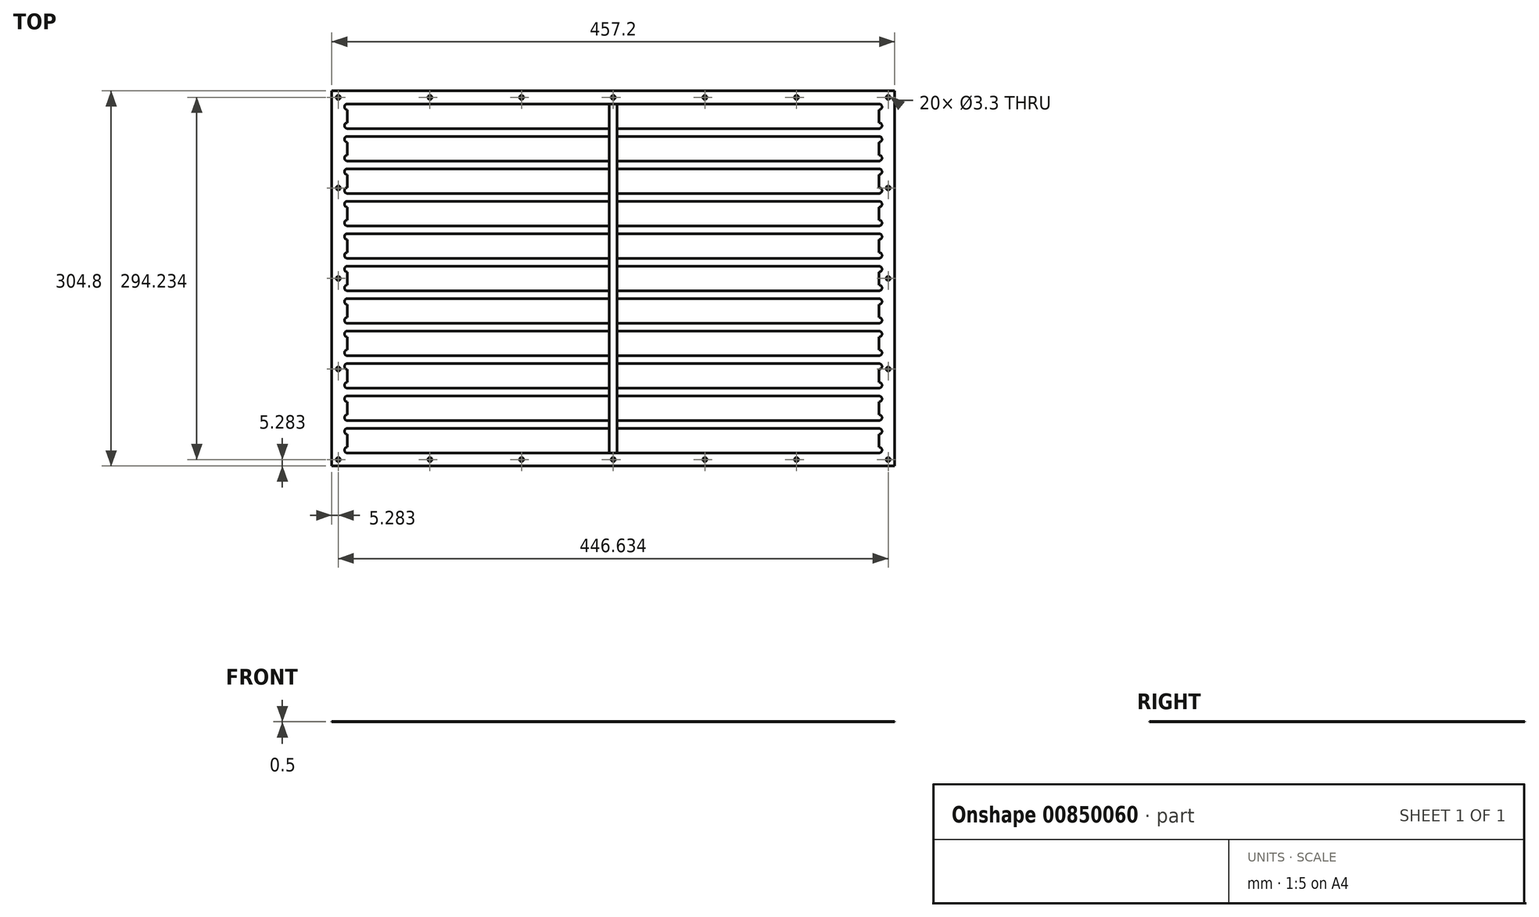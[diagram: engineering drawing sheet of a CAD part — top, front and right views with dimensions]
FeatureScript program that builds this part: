
annotation { "Feature Type Name" : "Feature", "Feature Type Description" : "" }
export const myFeature = defineFeature(function(context is Context, id is Id, definition is map)
    precondition{}
    {
        {
            assignVariable(context, id + "F0", {"name" : "mold_Thickness", "anyValue" : .5});
        }
        {
            assignVariable(context, id + "F1", {"name" : "hole_Depth", "anyValue" : .25});
        }
        {
            var Q0;
            Q0=qCreatedBy(makeId("Top.planeOp"),FACE);
            var sketch = newSketch(context, id + "F2", { "sketchPlane" : qUnion([Q0])});
            skLineSegment(sketch, "E0.bottom", {"start": v(228.6, -152.4) * mm, "end": v(-228.6, -152.4) * mm});
            skLineSegment(sketch, "E0.top", {"start": v(228.6, 152.4) * mm, "end": v(-228.6, 152.4) * mm});
            skLineSegment(sketch, "E0.left", {"start": v(228.6, -152.4) * mm, "end": v(228.6, 152.4) * mm});
            skLineSegment(sketch, "E0.right", {"start": v(-228.6, -152.4) * mm, "end": v(-228.6, 152.4) * mm});
            skPoint(sketch, "E0.middle", {"position": v(0, 0) * mm});
            skSolve(sketch);
        }
        {
            var Q0;
            Q0 = qSketchRegion(id + "F2", true);
            extrude(context, id + "F3", {"entities" : qUnion([Q0]), "depth" : (getVariable(context, 'mold_Thickness')) * mm, "offsetDistance" : 25.4 * mm});
        }
        {
            var Q0;
            Q0=makeQuery(id+"F3.opExtrude","CAP_FACE",FACE,{"disambiguationData":[OSD([sQuery(id+"F2.wireOp",EDGE,"E0.bottom"),sQuery(id+"F2.wireOp",EDGE,"E0.top"),sQuery(id+"F2.wireOp",EDGE,"E0.left"),sQuery(id+"F2.wireOp",EDGE,"E0.right")])],"isStart":false});
            var sketch = newSketch(context, id + "F4", { "sketchPlane" : qUnion([Q0])});
            skLineSegment(sketch, "E1.bottom", {"start": v(-215.9, 141.83) * mm, "end": v(215.9, 141.83) * mm});
            skLineSegment(sketch, "E1.top", {"start": v(-215.9, 121.82) * mm, "end": v(215.9, 121.82) * mm});
            skLineSegment(sketch, "E1.left", {"start": v(-215.9, 141.83) * mm, "end": v(-215.9, 121.82) * mm});
            skLineSegment(sketch, "E1.right", {"start": v(215.9, 141.83) * mm, "end": v(215.9, 121.82) * mm});
            skLineSegment(sketch, "E2.bottom", {"start": v(-215.9, 115.47) * mm, "end": v(215.9, 115.47) * mm});
            skLineSegment(sketch, "E2.top", {"start": v(-215.9, 95.45) * mm, "end": v(215.9, 95.45) * mm});
            skLineSegment(sketch, "E2.left", {"start": v(-215.9, 115.47) * mm, "end": v(-215.9, 95.45) * mm});
            skLineSegment(sketch, "E2.right", {"start": v(215.9, 115.47) * mm, "end": v(215.9, 95.45) * mm});
            skLineSegment(sketch, "E3.bottom", {"start": v(-215.9, 89.1) * mm, "end": v(215.9, 89.1) * mm});
            skLineSegment(sketch, "E3.top", {"start": v(-215.9, 69.09) * mm, "end": v(215.9, 69.09) * mm});
            skLineSegment(sketch, "E3.left", {"start": v(-215.9, 89.1) * mm, "end": v(-215.9, 69.09) * mm});
            skLineSegment(sketch, "E3.right", {"start": v(215.9, 89.1) * mm, "end": v(215.9, 69.09) * mm});
            skLineSegment(sketch, "E4.bottom", {"start": v(-215.9, 62.74) * mm, "end": v(215.9, 62.74) * mm});
            skLineSegment(sketch, "E4.top", {"start": v(-215.9, 42.72) * mm, "end": v(215.9, 42.72) * mm});
            skLineSegment(sketch, "E4.left", {"start": v(-215.9, 62.74) * mm, "end": v(-215.9, 42.72) * mm});
            skLineSegment(sketch, "E4.right", {"start": v(215.9, 62.74) * mm, "end": v(215.9, 42.72) * mm});
            skLineSegment(sketch, "E5.bottom", {"start": v(-215.9, 36.37) * mm, "end": v(215.9, 36.37) * mm});
            skLineSegment(sketch, "E5.top", {"start": v(-215.9, 16.36) * mm, "end": v(215.9, 16.36) * mm});
            skLineSegment(sketch, "E5.left", {"start": v(-215.9, 36.37) * mm, "end": v(-215.9, 16.36) * mm});
            skLineSegment(sketch, "E5.right", {"start": v(215.9, 36.37) * mm, "end": v(215.9, 16.36) * mm});
            skLineSegment(sketch, "E6.bottom", {"start": v(-215.9, 10) * mm, "end": v(215.9, 10) * mm});
            skLineSegment(sketch, "E6.top", {"start": v(-215.9, -10) * mm, "end": v(215.9, -10) * mm});
            skLineSegment(sketch, "E6.left", {"start": v(-215.9, 10) * mm, "end": v(-215.9, -10) * mm});
            skLineSegment(sketch, "E6.right", {"start": v(215.9, 10) * mm, "end": v(215.9, -10) * mm});
            skLineSegment(sketch, "E7.bottom", {"start": v(-215.9, -16.36) * mm, "end": v(215.9, -16.36) * mm});
            skLineSegment(sketch, "E7.top", {"start": v(-215.9, -36.37) * mm, "end": v(215.9, -36.37) * mm});
            skLineSegment(sketch, "E7.left", {"start": v(-215.9, -16.36) * mm, "end": v(-215.9, -36.37) * mm});
            skLineSegment(sketch, "E7.right", {"start": v(215.9, -16.36) * mm, "end": v(215.9, -36.37) * mm});
            skPoint(sketch, "E8.firstSnap0", {"position": v(-215.9, -26.37) * mm});
            skLineSegment(sketch, "E8.bottom", {"start": v(-215.9, -42.72) * mm, "end": v(215.9, -42.72) * mm});
            skLineSegment(sketch, "E8.top", {"start": v(-215.9, -62.74) * mm, "end": v(215.9, -62.74) * mm});
            skLineSegment(sketch, "E8.left", {"start": v(-215.9, -42.72) * mm, "end": v(-215.9, -62.74) * mm});
            skLineSegment(sketch, "E8.right", {"start": v(215.9, -42.72) * mm, "end": v(215.9, -62.74) * mm});
            skLineSegment(sketch, "E9.bottom", {"start": v(-215.9, -69.09) * mm, "end": v(215.9, -69.09) * mm});
            skLineSegment(sketch, "E9.top", {"start": v(-215.9, -89.1) * mm, "end": v(215.9, -89.1) * mm});
            skLineSegment(sketch, "E9.left", {"start": v(-215.9, -69.09) * mm, "end": v(-215.9, -89.1) * mm});
            skLineSegment(sketch, "E9.right", {"start": v(215.9, -69.09) * mm, "end": v(215.9, -89.1) * mm});
            skLineSegment(sketch, "E10.bottom", {"start": v(-215.9, -95.45) * mm, "end": v(215.9, -95.45) * mm});
            skLineSegment(sketch, "E10.top", {"start": v(-215.9, -115.47) * mm, "end": v(215.9, -115.47) * mm});
            skLineSegment(sketch, "E10.left", {"start": v(-215.9, -95.45) * mm, "end": v(-215.9, -115.47) * mm});
            skLineSegment(sketch, "E10.right", {"start": v(215.9, -95.45) * mm, "end": v(215.9, -115.47) * mm});
            skLineSegment(sketch, "E11.bottom", {"start": v(-215.9, -121.82) * mm, "end": v(215.9, -121.82) * mm});
            skLineSegment(sketch, "E11.top", {"start": v(-215.9, -141.83) * mm, "end": v(215.9, -141.83) * mm});
            skLineSegment(sketch, "E11.left", {"start": v(-215.9, -121.82) * mm, "end": v(-215.9, -141.83) * mm});
            skLineSegment(sketch, "E11.right", {"start": v(215.9, -121.82) * mm, "end": v(215.9, -141.83) * mm});
            skSolve(sketch);
        }
        {
            var Q0;
            Q0 = qSketchRegion(id + "F4", true);
            extrude(context, id + "F5", {"entities" : qUnion([Q0]), "operationType" : NewBodyOperationType.REMOVE, "oppositeDirection" : true, "depth" : (getVariable(context, 'hole_Depth')) * mm, "offsetDistance" : 25.4 * mm});
        }
        {
            var Q0;
            Q0=makeQuery(id+"F3.opExtrude","CAP_FACE",FACE,{"disambiguationData":[OSD([sQuery(id+"F2.wireOp",EDGE,"E0.bottom"),sQuery(id+"F2.wireOp",EDGE,"E0.top"),sQuery(id+"F2.wireOp",EDGE,"E0.left"),sQuery(id+"F2.wireOp",EDGE,"E0.right")])],"isStart":false});
            var sketch = newSketch(context, id + "F6", { "sketchPlane" : qUnion([Q0])});
            skLineSegment(sketch, "E12", {"start": v(-350.53, 0) * mm, "end": v(315.28, 0) * mm, "construction": true});
            skLineSegment(sketch, "E13", {"start": v(0, 183.28) * mm, "end": v(0, -194.06) * mm, "construction": true});
            skPoint(sketch, "E14", {"position": v(0, 147.12) * mm});
            skPoint(sketch, "E15", {"position": v(-74.44, 147.12) * mm});
            skPoint(sketch, "E16", {"position": v(-148.88, 147.12) * mm});
            skPoint(sketch, "E17", {"position": v(-223.32, 147.12) * mm});
            skPoint(sketch, "E18", {"position": v(-223.32, 73.56) * mm});
            skPoint(sketch, "E19", {"position": v(-223.32, 0) * mm});
            skPoint(sketch, "E20.MirrorP", {"position": v(74.44, 147.12) * mm});
            skPoint(sketch, "E21.MirrorP", {"position": v(148.88, 147.12) * mm});
            skPoint(sketch, "E22.MirrorP", {"position": v(223.32, 147.12) * mm});
            skPoint(sketch, "E23.MirrorP", {"position": v(223.32, 73.56) * mm});
            skPoint(sketch, "E24.MirrorP", {"position": v(223.32, 0) * mm});
            skPoint(sketch, "E25.MirrorP", {"position": v(-223.32, -73.56) * mm});
            skPoint(sketch, "E26.MirrorP", {"position": v(-223.32, -147.12) * mm});
            skPoint(sketch, "E27.MirrorP", {"position": v(-148.88, -147.12) * mm});
            skPoint(sketch, "E28.MirrorP", {"position": v(-74.44, -147.12) * mm});
            skPoint(sketch, "E29.MirrorP", {"position": v(0, -147.12) * mm});
            skPoint(sketch, "E30.MirrorP", {"position": v(74.44, -147.12) * mm});
            skPoint(sketch, "E31.MirrorP", {"position": v(148.88, -147.12) * mm});
            skPoint(sketch, "E32.MirrorP", {"position": v(223.32, -73.56) * mm});
            skPoint(sketch, "E33.MirrorP", {"position": v(223.32, -147.12) * mm});
            skSolve(sketch);
        }
        {
            var Q0;
            Q0=sQuery(id+"F6.wireOp",VERTEX,"E17");
            var Q1;
            Q1=sQuery(id+"F6.wireOp",VERTEX,"E18");
            var Q2;
            Q2=sQuery(id+"F6.wireOp",VERTEX,"E19");
            var Q3;
            Q3=sQuery(id+"F6.wireOp",VERTEX,"E25.MirrorP");
            var Q4;
            Q4=sQuery(id+"F6.wireOp",VERTEX,"E26.MirrorP");
            var Q5;
            Q5=sQuery(id+"F6.wireOp",VERTEX,"E27.MirrorP");
            var Q6;
            Q6=sQuery(id+"F6.wireOp",VERTEX,"E28.MirrorP");
            var Q7;
            Q7=sQuery(id+"F6.wireOp",VERTEX,"E29.MirrorP");
            var Q8;
            Q8=sQuery(id+"F6.wireOp",VERTEX,"E30.MirrorP");
            var Q9;
            Q9=sQuery(id+"F6.wireOp",VERTEX,"E31.MirrorP");
            var Q10;
            Q10=sQuery(id+"F6.wireOp",VERTEX,"E33.MirrorP");
            var Q11;
            Q11=sQuery(id+"F6.wireOp",VERTEX,"E32.MirrorP");
            var Q12;
            Q12=sQuery(id+"F6.wireOp",VERTEX,"E24.MirrorP");
            var Q13;
            Q13=sQuery(id+"F6.wireOp",VERTEX,"E23.MirrorP");
            var Q14;
            Q14=sQuery(id+"F6.wireOp",VERTEX,"E22.MirrorP");
            var Q15;
            Q15=sQuery(id+"F6.wireOp",VERTEX,"E21.MirrorP");
            var Q16;
            Q16=sQuery(id+"F6.wireOp",VERTEX,"E20.MirrorP");
            var Q17;
            Q17=sQuery(id+"F6.wireOp",VERTEX,"E14");
            var Q18;
            Q18=sQuery(id+"F6.wireOp",VERTEX,"E15");
            var Q19;
            Q19=sQuery(id+"F6.wireOp",VERTEX,"E16");
            var Q20;
            Q20=makeQuery(id+"F3.opExtrude","SWEPT_BODY",BODY,{"disambiguationData":[OSD([sQuery(id+"F2.wireOp",EDGE,"E0.bottom"),sQuery(id+"F2.wireOp",EDGE,"E0.top"),sQuery(id+"F2.wireOp",EDGE,"E0.left"),sQuery(id+"F2.wireOp",EDGE,"E0.right")])]});
            hole(context, id + "F7", {"style" : HoleStyle.SIMPLE, "endStyle" : HoleEndStyle.THROUGH, "standardTappedOrClearance" : lookupTablePath({ "standard" : "ISO", "engagement" : "75%", "pitch" : "0.7 mm", "size" : "M4", "type" : "Tapped" }), "standardBlindInLast" : lookupTablePath({ "standard" : "ISO", "engagement" : "75%", "pitch" : "0.7 mm", "size" : "M4", "type" : "Tapped" }), "holeDiameter" : 3.3 * mm, "majorDiameter" : 4 * mm, "showTappedDepth" : true, "isTappedThrough" : true, "tappedDepth" : 6.35 * mm, "tapClearance" : 3, "locations" : qUnion([Q0, Q1, Q2, Q3, Q4, Q5, Q6, Q7, Q8, Q9, Q10, Q11, Q12, Q13, Q14, Q15, Q16, Q17, Q18, Q19]), "scope" : qUnion([Q20])});
        }
        {
            var Q0;
            Q0=makeQuery(id+"F3.opExtrude","CAP_FACE",FACE,{"disambiguationData":[OSD([sQuery(id+"F2.wireOp",EDGE,"E0.bottom"),sQuery(id+"F2.wireOp",EDGE,"E0.top"),sQuery(id+"F2.wireOp",EDGE,"E0.left"),sQuery(id+"F2.wireOp",EDGE,"E0.right")])],"isStart":false});
            var sketch = newSketch(context, id + "F8", { "sketchPlane" : qUnion([Q0])});
            skCircle(sketch, "E34", {"center": v(-215.9, 33.99) * mm, "radius": 2.39 * mm});
            skCircle(sketch, "E35", {"center": v(-215.9, 45.11) * mm, "radius": 2.39 * mm});
            skCircle(sketch, "E36", {"center": v(-215.9, 60.35) * mm, "radius": 2.39 * mm});
            skCircle(sketch, "E37", {"center": v(-215.9, 86.72) * mm, "radius": 2.39 * mm});
            skCircle(sketch, "E38", {"center": v(-215.9, 71.48) * mm, "radius": 2.39 * mm});
            skCircle(sketch, "E39", {"center": v(-215.9, 97.84) * mm, "radius": 2.39 * mm});
            skCircle(sketch, "E40", {"center": v(-215.9, 113.08) * mm, "radius": 2.39 * mm});
            skCircle(sketch, "E41", {"center": v(-215.9, 124.2) * mm, "radius": 2.39 * mm});
            skCircle(sketch, "E42", {"center": v(-215.9, 139.45) * mm, "radius": 2.39 * mm});
            skCircle(sketch, "E43", {"center": v(-215.9, 18.75) * mm, "radius": 2.39 * mm});
            skCircle(sketch, "E44", {"center": v(-215.9, 7.62) * mm, "radius": 2.39 * mm});
            skLineSegment(sketch, "E45", {"start": v(-312.37, 0) * mm, "end": v(353.51, 0) * mm, "construction": true});
            skLineSegment(sketch, "E46", {"start": v(0, 219.79) * mm, "end": v(0, -191.65) * mm, "construction": true});
            skCircle(sketch, "E47.MirrorC", {"center": v(215.9, 7.62) * mm, "radius": 2.39 * mm});
            skCircle(sketch, "E48.MirrorC", {"center": v(215.9, 18.75) * mm, "radius": 2.39 * mm});
            skCircle(sketch, "E49.MirrorC", {"center": v(215.9, 33.99) * mm, "radius": 2.39 * mm});
            skCircle(sketch, "E50.MirrorC", {"center": v(215.9, 45.11) * mm, "radius": 2.39 * mm});
            skCircle(sketch, "E51.MirrorC", {"center": v(215.9, 60.35) * mm, "radius": 2.39 * mm});
            skCircle(sketch, "E52.MirrorC", {"center": v(215.9, 71.48) * mm, "radius": 2.39 * mm});
            skCircle(sketch, "E53.MirrorC", {"center": v(215.9, 86.72) * mm, "radius": 2.39 * mm});
            skCircle(sketch, "E54.MirrorC", {"center": v(215.9, 97.84) * mm, "radius": 2.39 * mm});
            skCircle(sketch, "E55.MirrorC", {"center": v(215.9, 113.08) * mm, "radius": 2.39 * mm});
            skCircle(sketch, "E56.MirrorC", {"center": v(215.9, 124.2) * mm, "radius": 2.39 * mm});
            skCircle(sketch, "E57.MirrorC", {"center": v(215.9, 139.45) * mm, "radius": 2.39 * mm});
            skCircle(sketch, "E58.MirrorC", {"center": v(215.9, -7.62) * mm, "radius": 2.39 * mm});
            skCircle(sketch, "E59.MirrorC", {"center": v(215.9, -18.75) * mm, "radius": 2.39 * mm});
            skCircle(sketch, "E60.MirrorC", {"center": v(215.9, -33.99) * mm, "radius": 2.39 * mm});
            skCircle(sketch, "E61.MirrorC", {"center": v(215.9, -45.11) * mm, "radius": 2.39 * mm});
            skCircle(sketch, "E62.MirrorC", {"center": v(215.9, -60.35) * mm, "radius": 2.39 * mm});
            skCircle(sketch, "E63.MirrorC", {"center": v(215.9, -71.48) * mm, "radius": 2.39 * mm});
            skCircle(sketch, "E64.MirrorC", {"center": v(215.9, -86.72) * mm, "radius": 2.39 * mm});
            skCircle(sketch, "E65.MirrorC", {"center": v(215.9, -97.84) * mm, "radius": 2.39 * mm});
            skCircle(sketch, "E66.MirrorC", {"center": v(215.9, -113.08) * mm, "radius": 2.39 * mm});
            skCircle(sketch, "E67.MirrorC", {"center": v(215.9, -124.2) * mm, "radius": 2.39 * mm});
            skCircle(sketch, "E68.MirrorC", {"center": v(215.9, -139.45) * mm, "radius": 2.39 * mm});
            skCircle(sketch, "E69.MirrorC", {"center": v(-215.9, -7.62) * mm, "radius": 2.39 * mm});
            skCircle(sketch, "E70.MirrorC", {"center": v(-215.9, -18.75) * mm, "radius": 2.39 * mm});
            skCircle(sketch, "E71.MirrorC", {"center": v(-215.9, -33.99) * mm, "radius": 2.39 * mm});
            skCircle(sketch, "E72.MirrorC", {"center": v(-215.9, -45.11) * mm, "radius": 2.39 * mm});
            skCircle(sketch, "E73.MirrorC", {"center": v(-215.9, -60.35) * mm, "radius": 2.39 * mm});
            skCircle(sketch, "E74.MirrorC", {"center": v(-215.9, -71.48) * mm, "radius": 2.39 * mm});
            skCircle(sketch, "E75.MirrorC", {"center": v(-215.9, -97.84) * mm, "radius": 2.39 * mm});
            skCircle(sketch, "E76.MirrorC", {"center": v(-215.9, -86.72) * mm, "radius": 2.39 * mm});
            skCircle(sketch, "E77.MirrorC", {"center": v(-215.9, -139.45) * mm, "radius": 2.39 * mm});
            skCircle(sketch, "E78.MirrorC", {"center": v(-215.9, -124.2) * mm, "radius": 2.39 * mm});
            skCircle(sketch, "E79.MirrorC", {"center": v(-215.9, -113.08) * mm, "radius": 2.39 * mm});
            skSolve(sketch);
        }
        {
            var Q0;
            Q0 = qSketchRegion(id + "F8", true);
            extrude(context, id + "F9", {"entities" : qUnion([Q0]), "operationType" : NewBodyOperationType.REMOVE, "oppositeDirection" : true, "depth" : (getVariable(context, 'hole_Depth')) * mm, "offsetDistance" : 25.4 * mm});
        }
        {
            var Q0;
            Q0=makeQuery(id+"F3.opExtrude","CAP_FACE",FACE,{"disambiguationData":[OSD([sQuery(id+"F2.wireOp",EDGE,"E0.bottom"),sQuery(id+"F2.wireOp",EDGE,"E0.top"),sQuery(id+"F2.wireOp",EDGE,"E0.left"),sQuery(id+"F2.wireOp",EDGE,"E0.right")])],"isStart":false});
            var sketch = newSketch(context, id + "F10", { "sketchPlane" : qUnion([Q0])});
            skLineSegment(sketch, "E80.bottom", {"start": v(3.18, -141.83) * mm, "end": v(-3.17, -141.83) * mm});
            skLineSegment(sketch, "E80.top", {"start": v(3.18, 141.83) * mm, "end": v(-3.17, 141.83) * mm});
            skLineSegment(sketch, "E80.left", {"start": v(3.18, -141.83) * mm, "end": v(3.18, 141.83) * mm});
            skLineSegment(sketch, "E80.right", {"start": v(-3.17, -141.83) * mm, "end": v(-3.17, 141.83) * mm});
            skPoint(sketch, "E80.middle", {"position": v(0, 0) * mm});
            skSolve(sketch);
        }
        {
            var Q0;
            Q0 = qSketchRegion(id + "F10", true);
            extrude(context, id + "F11", {"entities" : qUnion([Q0]), "operationType" : NewBodyOperationType.REMOVE, "oppositeDirection" : true, "depth" : 1.59 * mm, "offsetDistance" : 25.4 * mm});
        }
    });
